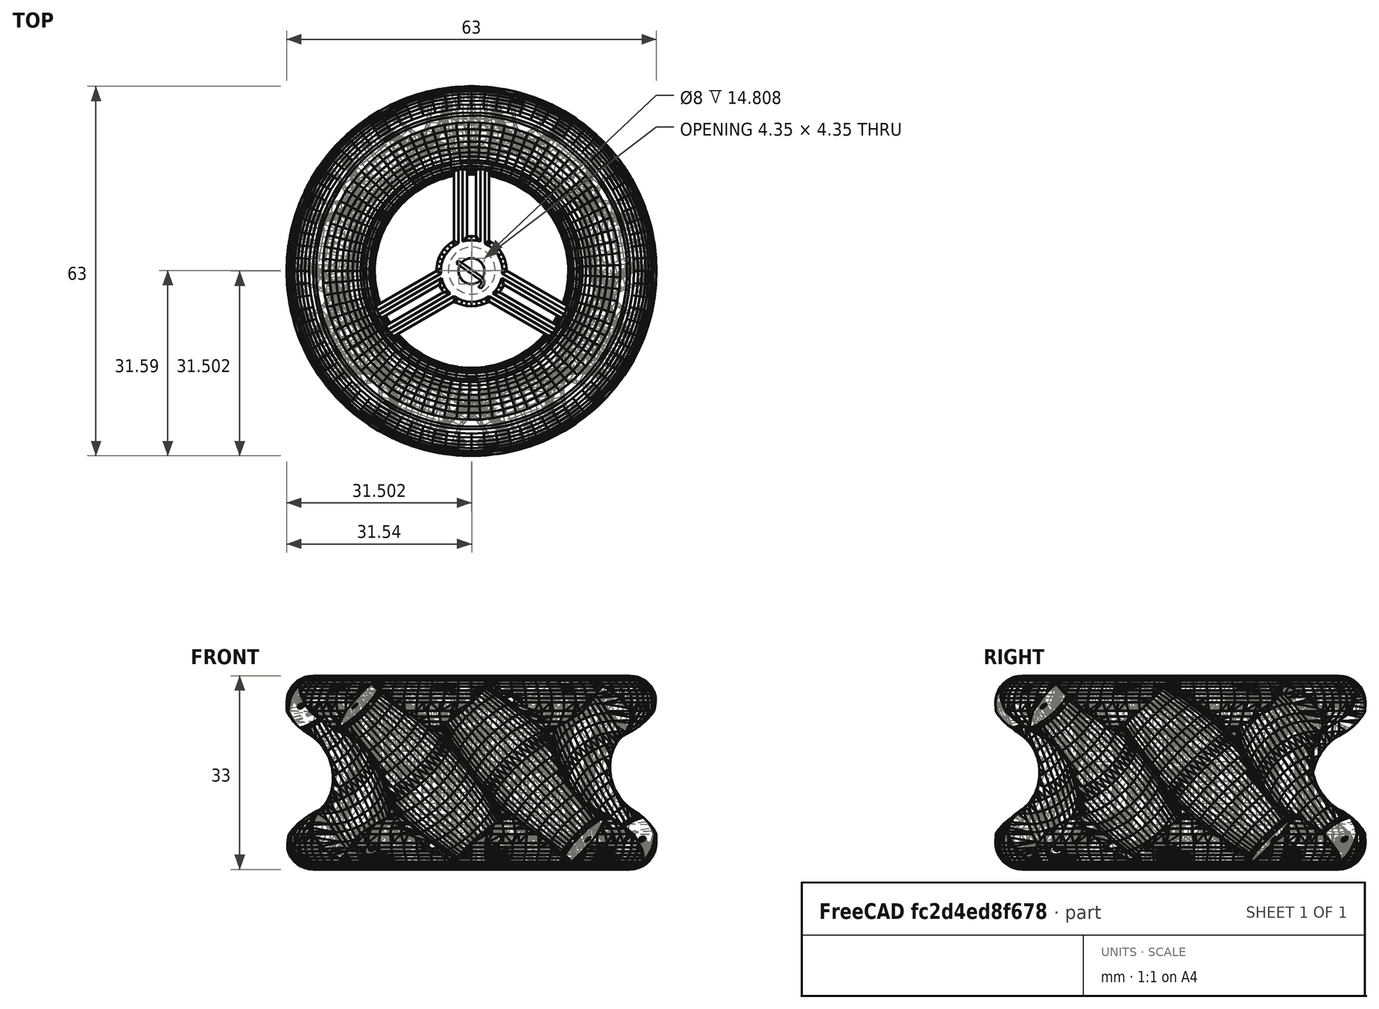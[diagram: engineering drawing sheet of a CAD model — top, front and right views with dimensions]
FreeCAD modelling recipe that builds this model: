
FCSTD DOCUMENT  (FreeCAD 0.17R13522 (Git))
Label: Body_Right.
License: All rights reserved
LicenseURL: http://en.wikipedia.org/wiki/All_rights_reserved
objects: Part::Cylinder×2, Part::Feature×1, Part::FeaturePython×1, Part::Cut×1, Part::Part2DObjectPython×1, Part::Extrusion×1, Mesh::Feature×1
note: 7 computed .brp shape members not serialized (recipe doc carries the construction recipe); baked Part::Feature solids carry a one-line shape summary decoded from their .brp

FEATURE [Part::Feature] Body_Right001_solid001  label="Body_Right001 (Solid)001"
  shape: large baked B-rep (30 MB .brp); summary skipped
FEATURE [Part::FeaturePython] Scale  # Draft clone (typed FeaturePython)
  Fuse = false
  Objects = -> [Body_Right001_solid001]
  Placement = pos=(-19.8232,-39.6639,-0.384298) rot=(0,0,1;0rad)
  Scale = (1.5,1.5,1.5)
FEATURE [Part::Cylinder] Cylinder  label="Cilindro"
  Angle = 360
  AttacherType = Attacher::AttachEngine3D
  Height = 20
  Placement = pos=(12.2,-6.5,-5) rot=(0,0,1;0rad)
  Radius = 4
FEATURE [Part::Cut] Cut
  Base = -> Scale
  Placement = pos=(0,0,5) rot=(0,0,1;0rad)
  Tool = -> Cylinder
FEATURE [Part::Cylinder] Cylinder001  label="Cilindro001"
  Angle = 360
  AttacherType = Attacher::AttachEngine3D
  Height = 10
  Placement = pos=(12.15,-6.6,19.2) rot=(0,0,1;0rad)
  Radius = 2.2
FEATURE [Part::Part2DObjectPython] ShapeString  # Draft 2D object (typed FeaturePython)
  FontFile = <path> medio teleco/segundo/impresiones/OpenSans-Regular.ttf
  Placement = pos=(13.5692,-9.46642,29.1922) rot=(0,0,1;0rad)
  Size = 6
  String = J
  Tracking = 0
FEATURE [Part::Extrusion] Extrude
  Base = -> ShapeString
  Dir = (0,0,1)
  DirMode = 2
  FaceMakerClass = Part::FaceMakerBullseye
  LengthFwd = 3
  LengthRev = 0
  Placement = pos=(-2.45,-14.15,-1) rot=(0,0,1;0.959931rad)
  Solid = false
  Symmetric = false
FEATURE [Mesh::Feature] enganche
  Placement = pos=(12.15,-6.6,0) rot=(0,0,1;0rad)
note: 1 file-system path scrubbed to <path> (originals preserved in the JSON sidecar)
